# Revit family: RLS2-LED-xxWS-xxxTx
name_source: partatom
category: Oprawy oświetleniowe
revit_build: Autodesk Revit 2017 (Build: 20190507_1515(x64)
units: mm (PartAtom-declared; Revit-internal decimal feet)

## family parameters
Numer OmniClass = 23.80.70.11
Obiekt nadrzędny = Powierzchnia
Punkt obliczania pomieszczeń = Nie
Tnij formami wycięć po wczytaniu = Nie
Typ części = Normalny
Tytuł OmniClass = Luminaries for Internal Lighting
Współdzielony = Nie
Wymiar okrągłego złącza = Użyj średnicy
Źródło światła = Tak

## types (8) — shared parameters
Emituj kształt widoczny w renderingu = Nie
Emituj ze średnicy okręgu = 285 mm  [stored 0.935039 ft]
Filtr koloru = 16777215
Kod zespołu = D5020200
Lampa = LED
Odchylenie kierunku = 90.00°
Producent = RIDI Leuchten GmbH
URL = www.ridi.de
Zmiana temperatury barwowej przyciemniania lampy = <Brak>
brand = RIDI
conformity mark = CE
electrical safety class = 1
height = 500 mm  [stored 1.64042 ft]
ingress protection (IP) code = IP65
length = 330 mm
nominal frequency = 50-60Hz
nominal voltage = 230
voltage type (AC, DC, UC) = AC
width = 330 mm
zero-valued in all types: Domyślna rzędna

## per-type parameters (varying)
| type | Model | Obciążenie pozorne | Plik sieci fotometrycznej | rated input power | weight |
| RLS2-LED NDWS-2200T840 | 0321487 | 170 VA | RLS2-LED NDWS-2200T840.IES | 170 | 9,2 kg |
| RLS2-LED DAWS-2200T840 | 0331487 | 170 VA | RLS2-LED NDWS-2200T840.IES | 170 | 9,4 kg |
| RLS2-LED NDWS-2200T865 | 0321488 | 170 VA | RLS2-LED NDWS-2200T840.IES | 170 | 9,2 kg |
| RLS2-LED DAWS-2200T865 | 0331488 | 170 VA | RLS2-LED NDWS-2200T840.IES | 170 | 9,4 kg |
| RLS2-LED NDWS-2800T840 | 0321485 | 237 VA | RLS2-LED NDWS-2800T840.IES | 237 | 9,2 kg |
| RLS2-LED DAWS-2800T840 | 0331485 | 237 VA | RLS2-LED NDWS-2800T840.IES | 237 | 9,4 kg |
| RLS2-LED NDWS-2800T865 | 0321486 | 237 VA | RLS2-LED NDWS-2800T840.IES | 237 | 9,2 kg |
| RLS2-LED DAWS-2800T865 | 0331486 | 237 VA | RLS2-LED NDWS-2800T840.IES | 237 | 9,4 kg |

note: column(s) folded — value = type name in every type: product name

note: [stored X ft] marks values corroborated as IEEE doubles in the binary element streams (Revit-internal decimal feet)
